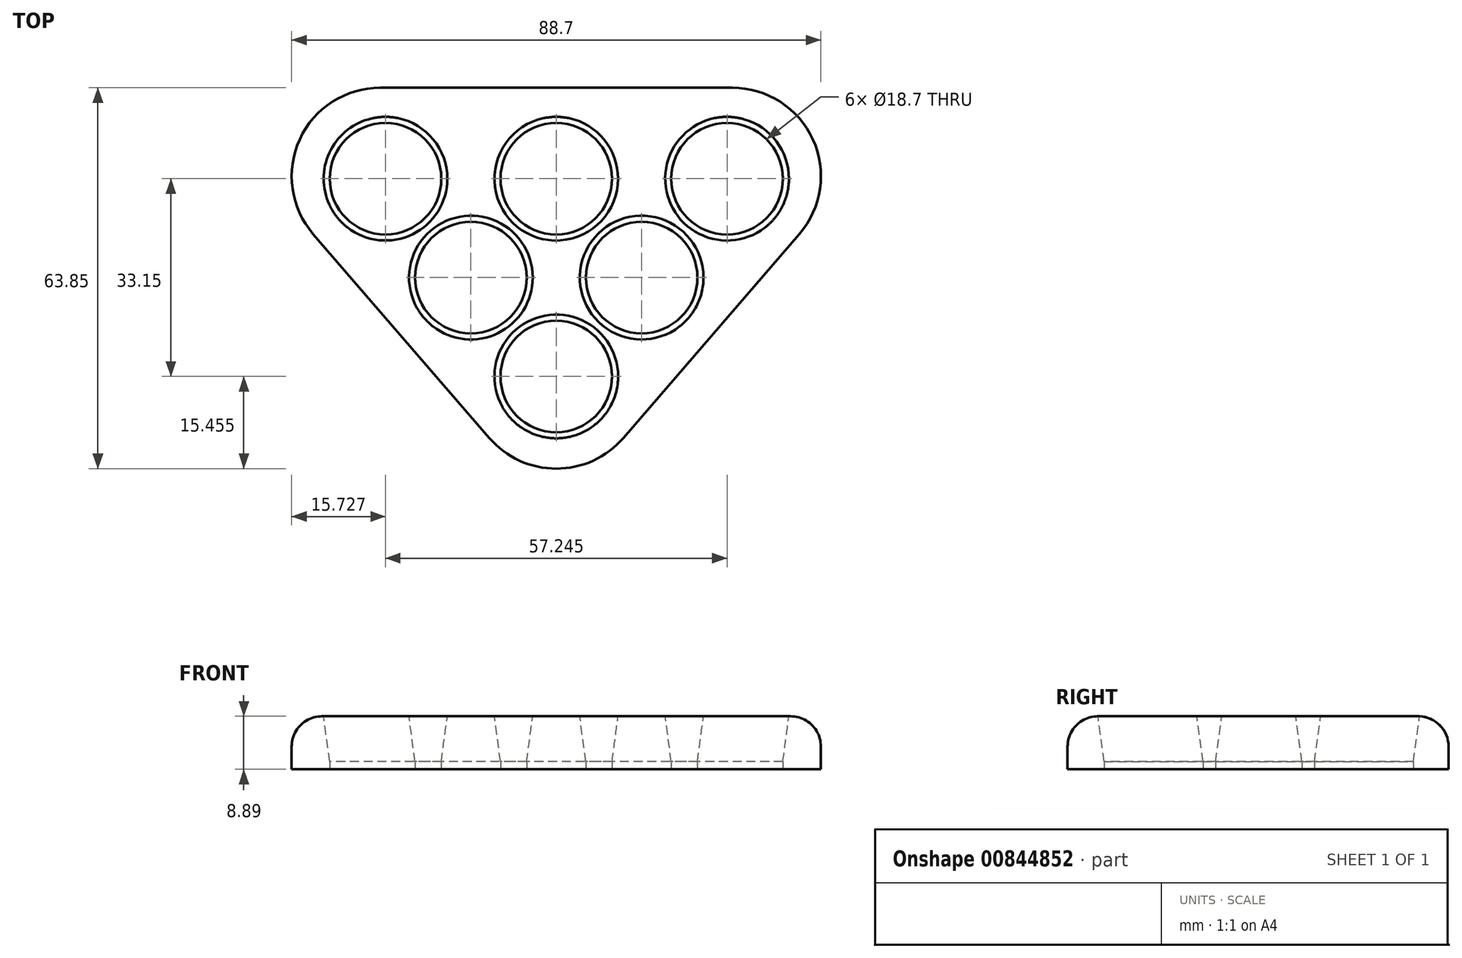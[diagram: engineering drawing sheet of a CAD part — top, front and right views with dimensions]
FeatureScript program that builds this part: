
annotation { "Feature Type Name" : "Feature", "Feature Type Description" : "" }
export const myFeature = defineFeature(function(context is Context, id is Id, definition is map)
    precondition{}
    {
        {
            var Q0;
            Q0=qCreatedBy(makeId("Top.planeOp"),FACE);
            var sketch = newSketch(context, id + "F0", { "sketchPlane" : qUnion([Q0])});
            skCircle(sketch, "E0", {"center": v(0, -16.58) * mm, "radius": 9.35 * mm});
            skCircle(sketch, "E1.MirrorC", {"center": v(0, 16.58) * mm, "radius": 9.35 * mm});
            skLineSegment(sketch, "E2", {"start": v(0, 16.58) * mm, "end": v(-28.62, 16.58) * mm, "construction": true});
            skLineSegment(sketch, "E3.MirrorCS", {"start": v(0, 16.58) * mm, "end": v(28.62, 16.58) * mm, "construction": true});
            skPoint(sketch, "E4", {"position": v(-14.31, 0) * mm});
            skCircle(sketch, "E5", {"center": v(-14.31, 0) * mm, "radius": 9.35 * mm});
            skLineSegment(sketch, "E6", {"start": v(0, -16.58) * mm, "end": v(-14.31, 0) * mm, "construction": true});
            skLineSegment(sketch, "E7", {"start": v(0, -16.58) * mm, "end": v(-6.1, -9.5) * mm});
            skCircle(sketch, "E8", {"center": v(-28.62, 16.58) * mm, "radius": 9.35 * mm});
            skCircle(sketch, "E9.MirrorC", {"center": v(14.31, 0) * mm, "radius": 9.35 * mm});
            skCircle(sketch, "E10.MirrorC", {"center": v(28.62, 16.58) * mm, "radius": 9.35 * mm});
            skLineSegment(sketch, "E11.MirrorCS", {"start": v(0, -16.58) * mm, "end": v(28.62, 16.58) * mm, "construction": true});
            skPoint(sketch, "E12.orphan", {"position": v(135.42, 16.58) * mm});
            skPoint(sketch, "E13.orphan", {"position": v(-135.42, 16.58) * mm});
            skLineSegment(sketch, "E14.trimOffspring", {"start": v(-14.31, 0) * mm, "end": v(-28.62, 16.58) * mm, "construction": true});
            skLineSegment(sketch, "E15.0", {"start": v(-35.36, 1.06) * mm, "end": v(-61.92, 31.82) * mm});
            skLineSegment(sketch, "E15.1", {"start": v(0, 31.82) * mm, "end": v(-61.92, 31.82) * mm});
            skLineSegment(sketch, "E15.2", {"start": v(0, -39.9) * mm, "end": v(-35.36, 1.06) * mm});
            skLineSegment(sketch, "E15.3", {"start": v(0, -39.9) * mm, "end": v(61.92, 31.82) * mm});
            skLineSegment(sketch, "E15.4", {"start": v(0, 31.82) * mm, "end": v(61.92, 31.82) * mm});
            skSolve(sketch);
        }
        {
            var Q0;
            Q0=makeQuery(id+"F0.imprint","IMPRINT",FACE,{"disambiguationData":[TD([[makeQuery(id+"F0.imprint","IMPRINT",EDGE,{"derivedFrom":sQuery(id+"F0.wireOp",EDGE,"oprLqbr8-PEwM-2erU-UPKV-yxrCI5EzFm7f")}),-1.0]])]});
            var Q1;
            Q1=makeQuery(id+"F0.imprint","IMPRINT",FACE,{"disambiguationData":[TD([[makeQuery(id+"F0.imprint","IMPRINT",EDGE,{"derivedFrom":sQuery(id+"F0.wireOp",EDGE,"E0")}),-1.0]])]});
            extrude(context, id + "F1", {"entities" : qUnion([Q0, Q1]), "depth" : 8.9 * mm, "offsetDistance" : 25.4 * mm});
        }
        {
            var Q0;
            Q0=makeQuery(id+"F1.opExtrude","SWEPT_EDGE",EDGE,{"disambiguationData":[OSD([sQuery(id+"F0.wireOp",EDGE,"E15.2"),sQuery(id+"F0.wireOp",EDGE,"E15.3")])]});
            var Q1;
            Q1=makeQuery(id+"F1.opExtrude","SWEPT_EDGE",EDGE,{"disambiguationData":[OSD([sQuery(id+"F0.wireOp",EDGE,"E15.0"),sQuery(id+"F0.wireOp",EDGE,"E15.1")])]});
            var Q2;
            Q2=makeQuery(id+"F1.opExtrude","SWEPT_EDGE",EDGE,{"disambiguationData":[OSD([sQuery(id+"F0.wireOp",EDGE,"E15.3"),sQuery(id+"F0.wireOp",EDGE,"E15.4")])]});
            fillet(context, id + "F2", {"entities" : qUnion([Q0, Q1, Q2]), "radius" : 14.83 * mm, "allowEdgeOverflow" : false});
        }
        {
            var Q0;
            Q0=makeQuery(id+"F1.opExtrude","CAP_EDGE",EDGE,{"disambiguationData":[OSD([sQuery(id+"F0.wireOp",EDGE,"E8")])],"isStart":false});
            var Q1;
            Q1=makeQuery(id+"F1.opExtrude","CAP_EDGE",EDGE,{"disambiguationData":[OSD([sQuery(id+"F0.wireOp",EDGE,"E5")])],"isStart":false});
            var Q2;
            Q2=makeQuery(id+"F1.opExtrude","CAP_EDGE",EDGE,{"disambiguationData":[OSD([sQuery(id+"F0.wireOp",EDGE,"E1.MirrorC")])],"isStart":false});
            var Q3;
            Q3=makeQuery(id+"F1.opExtrude","CAP_EDGE",EDGE,{"disambiguationData":[OSD([sQuery(id+"F0.wireOp",EDGE,"E9.MirrorC")])],"isStart":false});
            var Q4;
            Q4=makeQuery(id+"F1.opExtrude","CAP_EDGE",EDGE,{"disambiguationData":[OSD([sQuery(id+"F0.wireOp",EDGE,"E10.MirrorC")])],"isStart":false});
            var Q5;
            Q5=makeQuery(id+"F1.opExtrude","CAP_EDGE",EDGE,{"disambiguationData":[OSD([sQuery(id+"F0.wireOp",EDGE,"E0")])],"isStart":false});
            chamfer(context, id + "F3", {"entities" : qUnion([Q0, Q1, Q2, Q3, Q4, Q5]), "chamferType" : ChamferType.TWO_OFFSETS, "width1" : 7.62 * mm, "oppositeDirection" : false, "width2" : 1.02 * mm, "tangentPropagation" : true});
        }
        {
            var Q0;
            {var subQ0=sQuery(id+"F0.wireOp",EDGE,"E15.1");var subQ1=sQuery(id+"F0.wireOp",EDGE,"E15.0");Q0=makeQuery(id+"F2.opFillet","BLEND_EDGE",EDGE,{"blendedFrom":[makeQuery(id+"F1.opExtrude","SWEPT_EDGE",EDGE,{"disambiguationData":[OSD([subQ1,subQ0])]}),makeQuery(id+"F1.opExtrude","CAP_FACE",FACE,{"disambiguationData":[OSD([sQuery(id+"F0.wireOp",EDGE,"oprLqbr8-PEwM-2erU-UPKV-yxrCI5EzFm7f"),sQuery(id+"F0.wireOp",EDGE,"E0"),sQuery(id+"F0.wireOp",EDGE,"E1.MirrorC"),sQuery(id+"F0.wireOp",EDGE,"E5"),sQuery(id+"F0.wireOp",EDGE,"E8"),sQuery(id+"F0.wireOp",EDGE,"E9.MirrorC"),sQuery(id+"F0.wireOp",EDGE,"E10.MirrorC"),subQ1,subQ0,sQuery(id+"F0.wireOp",EDGE,"E15.2"),sQuery(id+"F0.wireOp",EDGE,"E15.3"),sQuery(id+"F0.wireOp",EDGE,"E15.4")])],"isStart":false})],"blendedInto":[makeQuery(id+"F1.opExtrude","CAP_FACE",FACE,{"disambiguationData":[OSD([sQuery(id+"F0.wireOp",EDGE,"oprLqbr8-PEwM-2erU-UPKV-yxrCI5EzFm7f"),sQuery(id+"F0.wireOp",EDGE,"E0"),sQuery(id+"F0.wireOp",EDGE,"E1.MirrorC"),sQuery(id+"F0.wireOp",EDGE,"E5"),sQuery(id+"F0.wireOp",EDGE,"E8"),sQuery(id+"F0.wireOp",EDGE,"E9.MirrorC"),sQuery(id+"F0.wireOp",EDGE,"E10.MirrorC"),subQ1,subQ0,sQuery(id+"F0.wireOp",EDGE,"E15.2"),sQuery(id+"F0.wireOp",EDGE,"E15.3"),sQuery(id+"F0.wireOp",EDGE,"E15.4")])],"isStart":false})]});}
            var Q1;
            Q1=makeQuery(id+"F1.opExtrude","CAP_EDGE",EDGE,{"disambiguationData":[OSD([sQuery(id+"F0.wireOp",EDGE,"E15.0"),sQuery(id+"F0.wireOp",EDGE,"E15.2")])],"isStart":false});
            var Q2;
            {var subQ0=sQuery(id+"F0.wireOp",EDGE,"E15.3");var subQ1=sQuery(id+"F0.wireOp",EDGE,"E15.2");Q2=makeQuery(id+"F2.opFillet","BLEND_EDGE",EDGE,{"blendedFrom":[makeQuery(id+"F1.opExtrude","SWEPT_EDGE",EDGE,{"disambiguationData":[OSD([subQ1,subQ0])]}),makeQuery(id+"F1.opExtrude","CAP_FACE",FACE,{"disambiguationData":[OSD([sQuery(id+"F0.wireOp",EDGE,"oprLqbr8-PEwM-2erU-UPKV-yxrCI5EzFm7f"),sQuery(id+"F0.wireOp",EDGE,"E0"),sQuery(id+"F0.wireOp",EDGE,"E1.MirrorC"),sQuery(id+"F0.wireOp",EDGE,"E5"),sQuery(id+"F0.wireOp",EDGE,"E8"),sQuery(id+"F0.wireOp",EDGE,"E9.MirrorC"),sQuery(id+"F0.wireOp",EDGE,"E10.MirrorC"),sQuery(id+"F0.wireOp",EDGE,"E15.0"),sQuery(id+"F0.wireOp",EDGE,"E15.1"),subQ1,subQ0,sQuery(id+"F0.wireOp",EDGE,"E15.4")])],"isStart":false})],"blendedInto":[makeQuery(id+"F1.opExtrude","CAP_FACE",FACE,{"disambiguationData":[OSD([sQuery(id+"F0.wireOp",EDGE,"oprLqbr8-PEwM-2erU-UPKV-yxrCI5EzFm7f"),sQuery(id+"F0.wireOp",EDGE,"E0"),sQuery(id+"F0.wireOp",EDGE,"E1.MirrorC"),sQuery(id+"F0.wireOp",EDGE,"E5"),sQuery(id+"F0.wireOp",EDGE,"E8"),sQuery(id+"F0.wireOp",EDGE,"E9.MirrorC"),sQuery(id+"F0.wireOp",EDGE,"E10.MirrorC"),sQuery(id+"F0.wireOp",EDGE,"E15.0"),sQuery(id+"F0.wireOp",EDGE,"E15.1"),subQ1,subQ0,sQuery(id+"F0.wireOp",EDGE,"E15.4")])],"isStart":false})]});}
            var Q3;
            Q3=makeQuery(id+"F1.opExtrude","CAP_EDGE",EDGE,{"disambiguationData":[OSD([sQuery(id+"F0.wireOp",EDGE,"E15.3")])],"isStart":false});
            var Q4;
            Q4=makeQuery(id+"F1.opExtrude","CAP_EDGE",EDGE,{"disambiguationData":[OSD([sQuery(id+"F0.wireOp",EDGE,"E15.1"),sQuery(id+"F0.wireOp",EDGE,"E15.4")])],"isStart":false});
            var Q5;
            {var subQ0=sQuery(id+"F0.wireOp",EDGE,"E15.4");var subQ1=sQuery(id+"F0.wireOp",EDGE,"E15.3");Q5=makeQuery(id+"F2.opFillet","BLEND_EDGE",EDGE,{"blendedFrom":[makeQuery(id+"F1.opExtrude","SWEPT_EDGE",EDGE,{"disambiguationData":[OSD([subQ1,subQ0])]}),makeQuery(id+"F1.opExtrude","CAP_FACE",FACE,{"disambiguationData":[OSD([sQuery(id+"F0.wireOp",EDGE,"oprLqbr8-PEwM-2erU-UPKV-yxrCI5EzFm7f"),sQuery(id+"F0.wireOp",EDGE,"E0"),sQuery(id+"F0.wireOp",EDGE,"E1.MirrorC"),sQuery(id+"F0.wireOp",EDGE,"E5"),sQuery(id+"F0.wireOp",EDGE,"E8"),sQuery(id+"F0.wireOp",EDGE,"E9.MirrorC"),sQuery(id+"F0.wireOp",EDGE,"E10.MirrorC"),sQuery(id+"F0.wireOp",EDGE,"E15.0"),sQuery(id+"F0.wireOp",EDGE,"E15.1"),sQuery(id+"F0.wireOp",EDGE,"E15.2"),subQ1,subQ0])],"isStart":false})],"blendedInto":[makeQuery(id+"F1.opExtrude","CAP_FACE",FACE,{"disambiguationData":[OSD([sQuery(id+"F0.wireOp",EDGE,"oprLqbr8-PEwM-2erU-UPKV-yxrCI5EzFm7f"),sQuery(id+"F0.wireOp",EDGE,"E0"),sQuery(id+"F0.wireOp",EDGE,"E1.MirrorC"),sQuery(id+"F0.wireOp",EDGE,"E5"),sQuery(id+"F0.wireOp",EDGE,"E8"),sQuery(id+"F0.wireOp",EDGE,"E9.MirrorC"),sQuery(id+"F0.wireOp",EDGE,"E10.MirrorC"),sQuery(id+"F0.wireOp",EDGE,"E15.0"),sQuery(id+"F0.wireOp",EDGE,"E15.1"),sQuery(id+"F0.wireOp",EDGE,"E15.2"),subQ1,subQ0])],"isStart":false})]});}
            fillet(context, id + "F4", {"entities" : qUnion([Q0, Q1, Q2, Q3, Q4, Q5]), "radius" : 5.08 * mm, "tangentPropagation" : true, "allowEdgeOverflow" : false});
        }
    });
